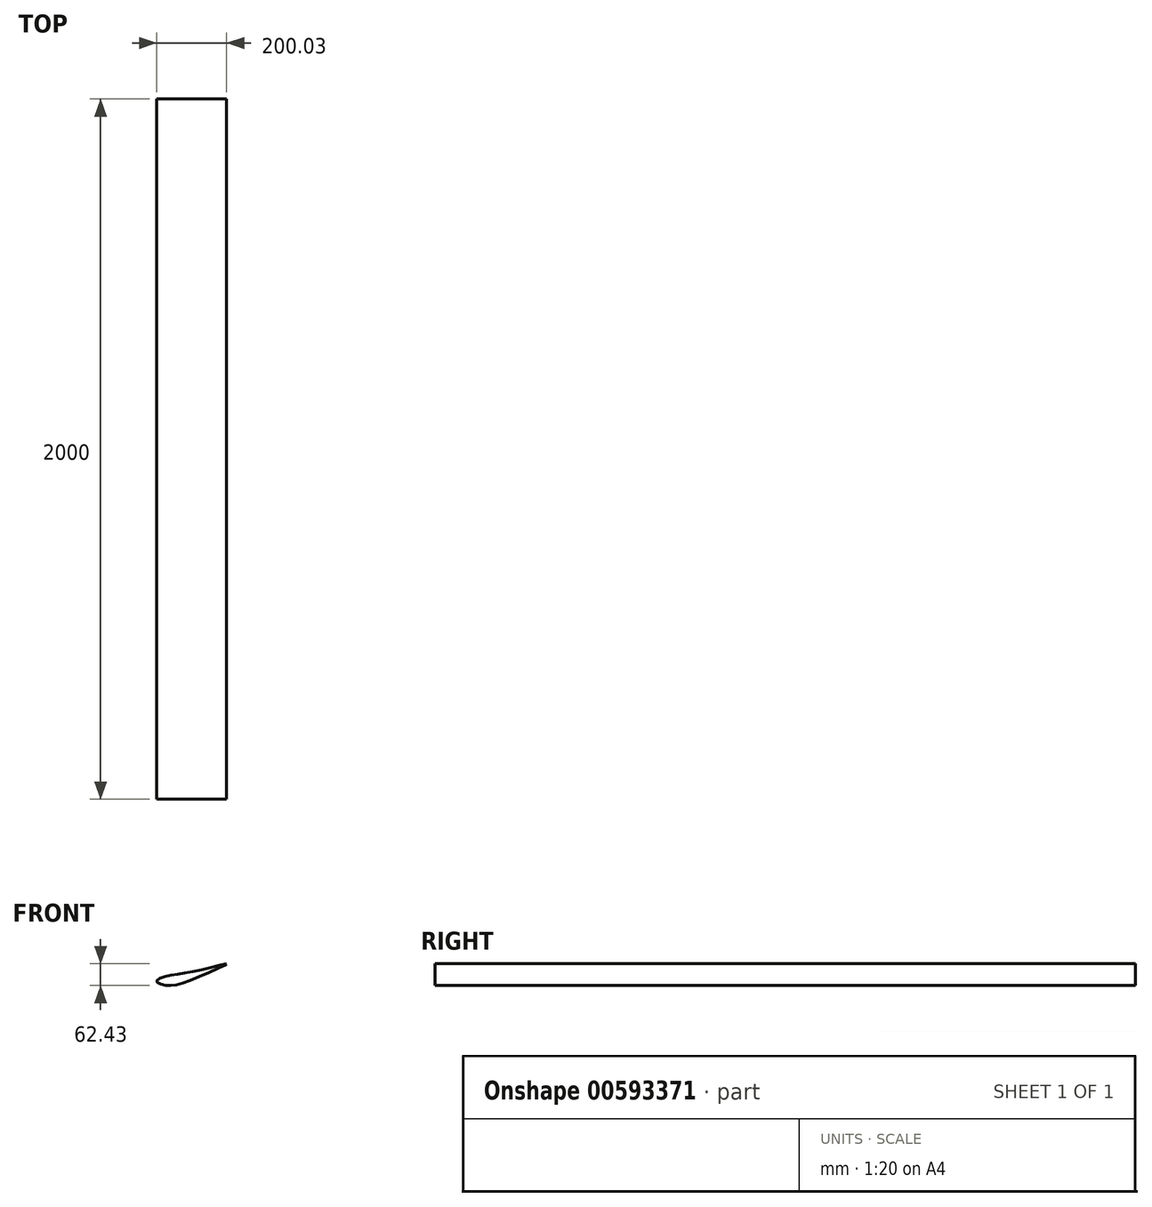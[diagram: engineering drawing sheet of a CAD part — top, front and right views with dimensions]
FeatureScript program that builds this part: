
annotation { "Feature Type Name" : "Feature", "Feature Type Description" : "" }
export const myFeature = defineFeature(function(context is Context, id is Id, definition is map)
    precondition{}
    {
        {
            var Q0;
            Q0=qCreatedBy(makeId("Front.planeOp"),FACE);
            var sketch = newSketch(context, id + "F0", { "sketchPlane" : qUnion([Q0])});
            skFitSpline(sketch, "E0", {"points": [v(0, 0) * mm, v(-79.2, -18.82) * mm, v(-175.26, -36.22) * mm, v(-200, -50) * mm, v(-175.02, -61.06) * mm, v(-108.4, -48.4) * mm, v(0, 0) * mm]});
            skSolve(sketch);
        }
        {
            var Q0;
            Q0 = qSketchRegion(id + "F0", true);
            extrude(context, id + "F1", {"entities" : qUnion([Q0]), "depth" : 2000 * mm, "offsetDistance" : 25.4 * mm});
        }
    });
